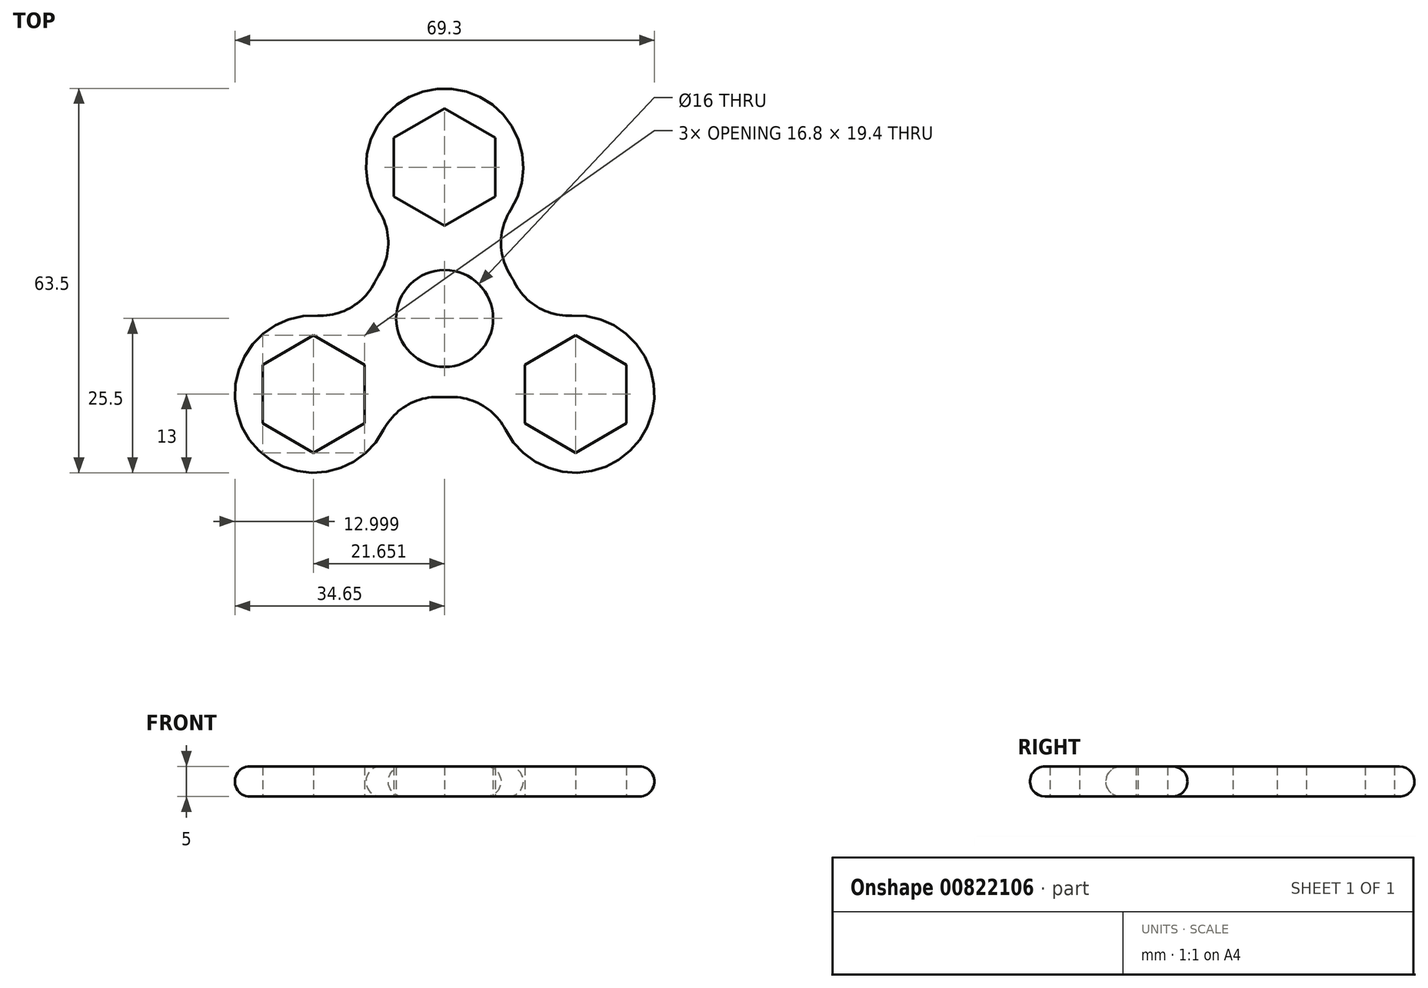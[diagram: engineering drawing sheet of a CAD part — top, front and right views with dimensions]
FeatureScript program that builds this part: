
annotation { "Feature Type Name" : "Feature", "Feature Type Description" : "" }
export const myFeature = defineFeature(function(context is Context, id is Id, definition is map)
    precondition{}
    {
        {
            var Q0;
            Q0=qCreatedBy(makeId("Top.planeOp"),FACE);
            var sketch = newSketch(context, id + "F0", { "sketchPlane" : qUnion([Q0])});
            skCircle(sketch, "E0", {"center": v(0, 0) * mm, "radius": 8 * mm});
            skCircle(sketch, "E1", {"center": v(0, 0) * mm, "radius": 25 * mm});
            skLineSegment(sketch, "E2", {"start": v(0, 0) * mm, "end": v(0, 45.5) * mm});
            skLineSegment(sketch, "E3", {"start": v(0, 0) * mm, "end": v(46, -26.56) * mm});
            skLineSegment(sketch, "E4", {"start": v(0, 0) * mm, "end": v(-45.6, -26.33) * mm});
            skCircle(sketch, "E5", {"center": v(0, 25) * mm, "radius": 13 * mm});
            skCircle(sketch, "E6", {"center": v(0, 0) * mm, "radius": 13 * mm});
            skCircle(sketch, "E7", {"center": v(-21.65, -12.5) * mm, "radius": 13 * mm});
            skCircle(sketch, "E8", {"center": v(21.65, -12.5) * mm, "radius": 13 * mm});
            skCircle(sketch, "E9.cCircle", {"center": v(-21.65, -12.5) * mm, "radius": 9.7 * mm, "construction": true});
            skLineSegment(sketch, "E9.0", {"start": v(-30.05, -17.35) * mm, "end": v(-30.05, -7.65) * mm});
            skLineSegment(sketch, "E9.1", {"start": v(-30.05, -7.65) * mm, "end": v(-21.65, -2.8) * mm});
            skLineSegment(sketch, "E9.2", {"start": v(-21.65, -2.8) * mm, "end": v(-13.25, -7.65) * mm});
            skLineSegment(sketch, "E9.3", {"start": v(-13.25, -7.65) * mm, "end": v(-13.25, -17.35) * mm});
            skLineSegment(sketch, "E9.4", {"start": v(-13.25, -17.35) * mm, "end": v(-21.65, -22.2) * mm});
            skLineSegment(sketch, "E9.5", {"start": v(-21.65, -22.2) * mm, "end": v(-30.05, -17.35) * mm});
            skLineSegment(sketch, "E10.1.0", {"start": v(30.05, -17.35) * mm, "end": v(21.65, -22.2) * mm});
            skLineSegment(sketch, "E10.1.1", {"start": v(21.65, -22.2) * mm, "end": v(13.25, -17.35) * mm});
            skLineSegment(sketch, "E10.1.2", {"start": v(13.25, -17.35) * mm, "end": v(13.25, -7.65) * mm});
            skLineSegment(sketch, "E10.1.3", {"start": v(13.25, -7.65) * mm, "end": v(21.65, -2.8) * mm});
            skLineSegment(sketch, "E10.1.4", {"start": v(21.65, -2.8) * mm, "end": v(30.05, -7.65) * mm});
            skLineSegment(sketch, "E10.1.5", {"start": v(30.05, -7.65) * mm, "end": v(30.05, -17.35) * mm});
            skLineSegment(sketch, "E10.2.0", {"start": v(0, 34.7) * mm, "end": v(8.4, 29.85) * mm});
            skLineSegment(sketch, "E10.2.1", {"start": v(8.4, 29.85) * mm, "end": v(8.4, 20.15) * mm});
            skLineSegment(sketch, "E10.2.2", {"start": v(8.4, 20.15) * mm, "end": v(0, 15.3) * mm});
            skLineSegment(sketch, "E10.2.3", {"start": v(0, 15.3) * mm, "end": v(-8.4, 20.15) * mm});
            skLineSegment(sketch, "E10.2.4", {"start": v(-8.4, 20.15) * mm, "end": v(-8.4, 29.85) * mm});
            skLineSegment(sketch, "E10.2.5", {"start": v(-8.4, 29.85) * mm, "end": v(0, 34.7) * mm});
            skCircle(sketch, "E11", {"center": v(0, 0) * mm, "radius": 38 * mm});
            skSolve(sketch);
        }
        {
            var Q0;
            {var subQ0=sQuery(id+"F0.wireOp",EDGE,"E4");var subQ1=sQuery(id+"F0.wireOp",EDGE,"E0");var subQ2=makeQuery(id+"F0.imprint","INTERSECT",VERTEX,{"derivedFrom":[subQ1,subQ0]});Q0=makeQuery(id+"F0.imprint","IMPRINT",FACE,{"disambiguationData":[TD([[makeQuery(id+"F0.imprint","IMPRINT",EDGE,{"disambiguationData":[TD([[subQ2,-1.0]])],"derivedFrom":subQ1}),-1.0]])]});}
            var Q1;
            {var subQ0=sQuery(id+"F0.wireOp",EDGE,"E9.3");Q1=makeQuery(id+"F0.imprint","IMPRINT",FACE,{"disambiguationData":[TD([[makeQuery(id+"F0.imprint","IMPRINT",EDGE,{"derivedFrom":subQ0}),1.0]])]});}
            var Q2;
            {var subQ0=sQuery(id+"F0.wireOp",EDGE,"E9.2");Q2=makeQuery(id+"F0.imprint","IMPRINT",FACE,{"disambiguationData":[TD([[makeQuery(id+"F0.imprint","IMPRINT",EDGE,{"derivedFrom":subQ0}),1.0]])]});}
            var Q3;
            {var subQ0=sQuery(id+"F0.wireOp",EDGE,"E9.0");Q3=makeQuery(id+"F0.imprint","IMPRINT",FACE,{"disambiguationData":[TD([[makeQuery(id+"F0.imprint","IMPRINT",EDGE,{"derivedFrom":subQ0}),1.0]])]});}
            var Q4;
            {var subQ0=sQuery(id+"F0.wireOp",EDGE,"E9.5");Q4=makeQuery(id+"F0.imprint","IMPRINT",FACE,{"disambiguationData":[TD([[makeQuery(id+"F0.imprint","IMPRINT",EDGE,{"derivedFrom":subQ0}),1.0]])]});}
            var Q5;
            {var subQ0=sQuery(id+"F0.wireOp",EDGE,"E10.1.2");Q5=makeQuery(id+"F0.imprint","IMPRINT",FACE,{"disambiguationData":[TD([[makeQuery(id+"F0.imprint","IMPRINT",EDGE,{"derivedFrom":subQ0}),1.0]])]});}
            var Q6;
            {var subQ0=sQuery(id+"F0.wireOp",EDGE,"E10.1.0");Q6=makeQuery(id+"F0.imprint","IMPRINT",FACE,{"disambiguationData":[TD([[makeQuery(id+"F0.imprint","IMPRINT",EDGE,{"derivedFrom":subQ0}),1.0]])]});}
            var Q7;
            {var subQ0=sQuery(id+"F0.wireOp",EDGE,"E10.1.5");Q7=makeQuery(id+"F0.imprint","IMPRINT",FACE,{"disambiguationData":[TD([[makeQuery(id+"F0.imprint","IMPRINT",EDGE,{"derivedFrom":subQ0}),1.0]])]});}
            var Q8;
            {var subQ0=sQuery(id+"F0.wireOp",EDGE,"E10.1.3");Q8=makeQuery(id+"F0.imprint","IMPRINT",FACE,{"disambiguationData":[TD([[makeQuery(id+"F0.imprint","IMPRINT",EDGE,{"derivedFrom":subQ0}),1.0]])]});}
            var Q9;
            {var subQ0=sQuery(id+"F0.wireOp",EDGE,"E2");var subQ1=sQuery(id+"F0.wireOp",EDGE,"E0");var subQ2=makeQuery(id+"F0.imprint","INTERSECT",VERTEX,{"derivedFrom":[subQ1,subQ0]});Q9=makeQuery(id+"F0.imprint","IMPRINT",FACE,{"disambiguationData":[TD([[makeQuery(id+"F0.imprint","IMPRINT",EDGE,{"disambiguationData":[TD([[subQ2,1.0]])],"derivedFrom":subQ1}),-1.0]])]});}
            var Q10;
            {var subQ0=sQuery(id+"F0.wireOp",EDGE,"E4");var subQ1=sQuery(id+"F0.wireOp",EDGE,"E0");var subQ2=makeQuery(id+"F0.imprint","INTERSECT",VERTEX,{"derivedFrom":[subQ1,subQ0]});Q10=makeQuery(id+"F0.imprint","IMPRINT",FACE,{"disambiguationData":[TD([[makeQuery(id+"F0.imprint","IMPRINT",EDGE,{"disambiguationData":[TD([[subQ2,1.0]])],"derivedFrom":subQ1}),-1.0]])]});}
            var Q11;
            {var subQ0=sQuery(id+"F0.wireOp",EDGE,"E10.2.2");Q11=makeQuery(id+"F0.imprint","IMPRINT",FACE,{"disambiguationData":[TD([[makeQuery(id+"F0.imprint","IMPRINT",EDGE,{"derivedFrom":subQ0}),1.0]])]});}
            var Q12;
            {var subQ0=sQuery(id+"F0.wireOp",EDGE,"E10.2.0");Q12=makeQuery(id+"F0.imprint","IMPRINT",FACE,{"disambiguationData":[TD([[makeQuery(id+"F0.imprint","IMPRINT",EDGE,{"derivedFrom":subQ0}),1.0]])]});}
            var Q13;
            {var subQ5=sQuery(id+"F0.wireOp",EDGE,"E10.2.3");Q13=makeQuery(id+"F0.imprint","IMPRINT",FACE,{"disambiguationData":[TD([[makeQuery(id+"F0.imprint","IMPRINT",EDGE,{"derivedFrom":subQ5}),1.0]])]});}
            var Q14;
            {var subQ0=sQuery(id+"F0.wireOp",EDGE,"E10.2.5");Q14=makeQuery(id+"F0.imprint","IMPRINT",FACE,{"disambiguationData":[TD([[makeQuery(id+"F0.imprint","IMPRINT",EDGE,{"derivedFrom":subQ0}),1.0]])]});}
            var Q15;
            {var subQ0=sQuery(id+"F0.wireOp",EDGE,"E7");var subQ1=sQuery(id+"F0.wireOp",EDGE,"E4");var subQ2=makeQuery(id+"F0.imprint","INTERSECT",VERTEX,{"disambiguationData":[OD(1.0)],"derivedFrom":[subQ1,subQ0]});Q15=makeQuery(id+"F0.imprint","IMPRINT",FACE,{"disambiguationData":[TD([[makeQuery(id+"F0.imprint","IMPRINT",EDGE,{"disambiguationData":[TD([[subQ2,-1.0]])],"derivedFrom":subQ1}),-1.0]])]});}
            var Q16;
            {var subQ0=sQuery(id+"F0.wireOp",EDGE,"E8");var subQ1=sQuery(id+"F0.wireOp",EDGE,"E3");var subQ2=makeQuery(id+"F0.imprint","INTERSECT",VERTEX,{"disambiguationData":[OD(1.0)],"derivedFrom":[subQ1,subQ0]});Q16=makeQuery(id+"F0.imprint","IMPRINT",FACE,{"disambiguationData":[TD([[makeQuery(id+"F0.imprint","IMPRINT",EDGE,{"disambiguationData":[TD([[subQ2,-1.0]])],"derivedFrom":subQ1}),-1.0]])]});}
            var Q17;
            {var subQ0=sQuery(id+"F0.wireOp",EDGE,"E8");var subQ1=sQuery(id+"F0.wireOp",EDGE,"E3");var subQ2=makeQuery(id+"F0.imprint","INTERSECT",VERTEX,{"disambiguationData":[OD(1.0)],"derivedFrom":[subQ1,subQ0]});Q17=makeQuery(id+"F0.imprint","IMPRINT",FACE,{"disambiguationData":[TD([[makeQuery(id+"F0.imprint","IMPRINT",EDGE,{"disambiguationData":[TD([[subQ2,-1.0]])],"derivedFrom":subQ1}),1.0]])]});}
            var Q18;
            {var subQ0=sQuery(id+"F0.wireOp",EDGE,"E7");var subQ1=sQuery(id+"F0.wireOp",EDGE,"E4");var subQ2=makeQuery(id+"F0.imprint","INTERSECT",VERTEX,{"disambiguationData":[OD(1.0)],"derivedFrom":[subQ1,subQ0]});Q18=makeQuery(id+"F0.imprint","IMPRINT",FACE,{"disambiguationData":[TD([[makeQuery(id+"F0.imprint","IMPRINT",EDGE,{"disambiguationData":[TD([[subQ2,-1.0]])],"derivedFrom":subQ1}),1.0]])]});}
            var Q19;
            {var subQ0=sQuery(id+"F0.wireOp",EDGE,"E5");var subQ1=sQuery(id+"F0.wireOp",EDGE,"E2");var subQ2=makeQuery(id+"F0.imprint","INTERSECT",VERTEX,{"disambiguationData":[OD(1.0)],"derivedFrom":[subQ1,subQ0]});Q19=makeQuery(id+"F0.imprint","IMPRINT",FACE,{"disambiguationData":[TD([[makeQuery(id+"F0.imprint","IMPRINT",EDGE,{"disambiguationData":[TD([[subQ2,-1.0]])],"derivedFrom":subQ1}),1.0]])]});}
            var Q20;
            {var subQ0=sQuery(id+"F0.wireOp",EDGE,"E5");var subQ1=sQuery(id+"F0.wireOp",EDGE,"E2");var subQ2=makeQuery(id+"F0.imprint","INTERSECT",VERTEX,{"disambiguationData":[OD(1.0)],"derivedFrom":[subQ1,subQ0]});Q20=makeQuery(id+"F0.imprint","IMPRINT",FACE,{"disambiguationData":[TD([[makeQuery(id+"F0.imprint","IMPRINT",EDGE,{"disambiguationData":[TD([[subQ2,-1.0]])],"derivedFrom":subQ1}),-1.0]])]});}
            extrude(context, id + "F1", {"entities" : qUnion([Q0, Q1, Q2, Q3, Q4, Q5, Q6, Q7, Q8, Q9, Q10, Q11, Q12, Q13, Q14, Q15, Q16, Q17, Q18, Q19, Q20]), "depth" : 5 * mm, "offsetDistance" : 25 * mm});
        }
        {
            var Q0;
            {var subQ0=sQuery(id+"F0.wireOp",EDGE,"E7");var subQ1=sQuery(id+"F0.wireOp",EDGE,"E6");Q0=makeQuery(id+"F1.opExtrude","SWEPT_EDGE",EDGE,{"disambiguationData":[OSD([subQ1,subQ0]),TDD([makeQuery(id+"F0.imprint","INTERSECT",VERTEX,{"disambiguationData":[OD(1.0)],"derivedFrom":[subQ1,subQ0]})])]});}
            var Q1;
            {var subQ0=sQuery(id+"F0.wireOp",EDGE,"E8");var subQ1=sQuery(id+"F0.wireOp",EDGE,"E6");Q1=makeQuery(id+"F1.opExtrude","SWEPT_EDGE",EDGE,{"disambiguationData":[OSD([subQ1,subQ0]),TDD([makeQuery(id+"F0.imprint","INTERSECT",VERTEX,{"disambiguationData":[OD(0.0)],"derivedFrom":[subQ1,subQ0]})])]});}
            var Q2;
            {var subQ0=sQuery(id+"F0.wireOp",EDGE,"E7");var subQ1=sQuery(id+"F0.wireOp",EDGE,"E6");Q2=makeQuery(id+"F1.opExtrude","SWEPT_EDGE",EDGE,{"disambiguationData":[OSD([subQ1,subQ0]),TDD([makeQuery(id+"F0.imprint","INTERSECT",VERTEX,{"disambiguationData":[OD(0.0)],"derivedFrom":[subQ1,subQ0]})])]});}
            var Q3;
            {var subQ0=sQuery(id+"F0.wireOp",EDGE,"E6");var subQ1=sQuery(id+"F0.wireOp",EDGE,"E5");Q3=makeQuery(id+"F1.opExtrude","SWEPT_EDGE",EDGE,{"disambiguationData":[OSD([subQ1,subQ0]),TDD([makeQuery(id+"F0.imprint","INTERSECT",VERTEX,{"disambiguationData":[OD(0.0)],"derivedFrom":[subQ1,subQ0]})])]});}
            var Q4;
            {var subQ0=sQuery(id+"F0.wireOp",EDGE,"E6");var subQ1=sQuery(id+"F0.wireOp",EDGE,"E5");Q4=makeQuery(id+"F1.opExtrude","SWEPT_EDGE",EDGE,{"disambiguationData":[OSD([subQ1,subQ0]),TDD([makeQuery(id+"F0.imprint","INTERSECT",VERTEX,{"disambiguationData":[OD(1.0)],"derivedFrom":[subQ1,subQ0]})])]});}
            var Q5;
            {var subQ0=sQuery(id+"F0.wireOp",EDGE,"E8");var subQ1=sQuery(id+"F0.wireOp",EDGE,"E6");Q5=makeQuery(id+"F1.opExtrude","SWEPT_EDGE",EDGE,{"disambiguationData":[OSD([subQ1,subQ0]),TDD([makeQuery(id+"F0.imprint","INTERSECT",VERTEX,{"disambiguationData":[OD(1.0)],"derivedFrom":[subQ1,subQ0]})])]});}
            fillet(context, id + "F2", {"entities" : qUnion([Q0, Q1, Q2, Q3, Q4, Q5]), "radius" : 10 * mm, "tangentPropagation" : true, "allowEdgeOverflow" : false});
        }
        {
            var Q0;
            Q0=makeQuery(id+"F1.opExtrude","CAP_EDGE",EDGE,{"disambiguationData":[OSD([sQuery(id+"F0.wireOp",EDGE,"E5")])],"isStart":false});
            var Q1;
            {var subQ0=sQuery(id+"F0.wireOp",EDGE,"E6");var subQ1=sQuery(id+"F0.wireOp",EDGE,"E5");Q1=makeQuery(id+"F2.opFillet","BLEND_EDGE",EDGE,{"blendedFrom":[makeQuery(id+"F1.opExtrude","SWEPT_EDGE",EDGE,{"disambiguationData":[OSD([subQ1,subQ0]),TDD([makeQuery(id+"F0.imprint","INTERSECT",VERTEX,{"disambiguationData":[OD(0.0)],"derivedFrom":[subQ1,subQ0]})])]}),makeQuery(id+"F1.opExtrude","CAP_FACE",FACE,{"disambiguationData":[OSD([sQuery(id+"F0.wireOp",EDGE,"E0"),subQ1,subQ0,sQuery(id+"F0.wireOp",EDGE,"E7"),sQuery(id+"F0.wireOp",EDGE,"E8"),sQuery(id+"F0.wireOp",EDGE,"E9.0"),sQuery(id+"F0.wireOp",EDGE,"E9.1"),sQuery(id+"F0.wireOp",EDGE,"E9.2"),sQuery(id+"F0.wireOp",EDGE,"E9.3"),sQuery(id+"F0.wireOp",EDGE,"E9.4"),sQuery(id+"F0.wireOp",EDGE,"E9.5"),sQuery(id+"F0.wireOp",EDGE,"E10.1.0"),sQuery(id+"F0.wireOp",EDGE,"E10.1.1"),sQuery(id+"F0.wireOp",EDGE,"E10.1.2"),sQuery(id+"F0.wireOp",EDGE,"E10.1.3"),sQuery(id+"F0.wireOp",EDGE,"E10.1.4"),sQuery(id+"F0.wireOp",EDGE,"E10.1.5"),sQuery(id+"F0.wireOp",EDGE,"E10.2.0"),sQuery(id+"F0.wireOp",EDGE,"E10.2.1"),sQuery(id+"F0.wireOp",EDGE,"E10.2.2"),sQuery(id+"F0.wireOp",EDGE,"E10.2.3"),sQuery(id+"F0.wireOp",EDGE,"E10.2.4"),sQuery(id+"F0.wireOp",EDGE,"E10.2.5")])],"isStart":false})],"blendedInto":[makeQuery(id+"F1.opExtrude","CAP_FACE",FACE,{"disambiguationData":[OSD([sQuery(id+"F0.wireOp",EDGE,"E0"),subQ1,subQ0,sQuery(id+"F0.wireOp",EDGE,"E7"),sQuery(id+"F0.wireOp",EDGE,"E8"),sQuery(id+"F0.wireOp",EDGE,"E9.0"),sQuery(id+"F0.wireOp",EDGE,"E9.1"),sQuery(id+"F0.wireOp",EDGE,"E9.2"),sQuery(id+"F0.wireOp",EDGE,"E9.3"),sQuery(id+"F0.wireOp",EDGE,"E9.4"),sQuery(id+"F0.wireOp",EDGE,"E9.5"),sQuery(id+"F0.wireOp",EDGE,"E10.1.0"),sQuery(id+"F0.wireOp",EDGE,"E10.1.1"),sQuery(id+"F0.wireOp",EDGE,"E10.1.2"),sQuery(id+"F0.wireOp",EDGE,"E10.1.3"),sQuery(id+"F0.wireOp",EDGE,"E10.1.4"),sQuery(id+"F0.wireOp",EDGE,"E10.1.5"),sQuery(id+"F0.wireOp",EDGE,"E10.2.0"),sQuery(id+"F0.wireOp",EDGE,"E10.2.1"),sQuery(id+"F0.wireOp",EDGE,"E10.2.2"),sQuery(id+"F0.wireOp",EDGE,"E10.2.3"),sQuery(id+"F0.wireOp",EDGE,"E10.2.4"),sQuery(id+"F0.wireOp",EDGE,"E10.2.5")])],"isStart":false})]});}
            var Q2;
            Q2=makeQuery(id+"F1.opExtrude","CAP_EDGE",EDGE,{"disambiguationData":[OSD([sQuery(id+"F0.wireOp",EDGE,"E7")])],"isStart":true});
            fillet(context, id + "F3", {"entities" : qUnion([Q0, Q1, Q2]), "radius" : 2.5 * mm, "tangentPropagation" : true, "allowEdgeOverflow" : false});
        }
    });
